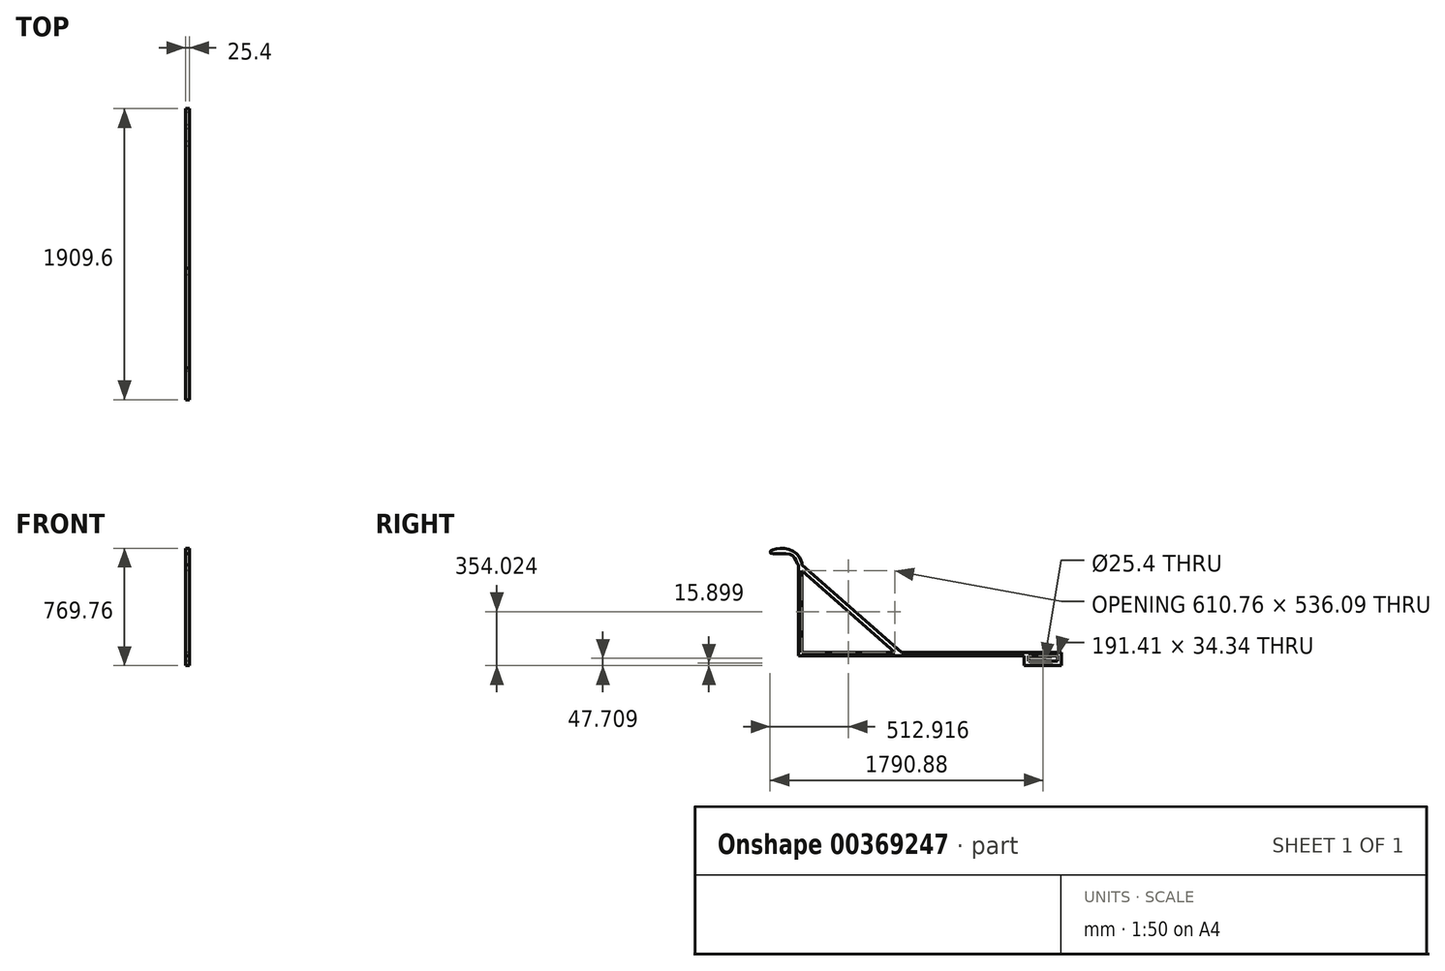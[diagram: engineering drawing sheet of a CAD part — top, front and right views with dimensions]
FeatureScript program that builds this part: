
annotation { "Feature Type Name" : "Feature", "Feature Type Description" : "" }
export const myFeature = defineFeature(function(context is Context, id is Id, definition is map)
    precondition{}
    {
        {
            var Q0;
            Q0=qCreatedBy(makeId("Right.planeOp"),FACE);
            var sketch = newSketch(context, id + "F0", { "sketchPlane" : qUnion([Q0])});
            skLineSegment(sketch, "E0.bottom", {"start": v(-864.8, -69.1) * mm, "end": v(613.39, -69.1) * mm});
            skLineSegment(sketch, "E0.top", {"start": v(-843.71, -48) * mm, "end": v(-232.95, -48) * mm});
            skLineSegment(sketch, "E0.left", {"start": v(-864.8, -69.1) * mm, "end": v(-864.8, -48) * mm});
            skLineSegment(sketch, "E0.right", {"start": v(858.35, -69.1) * mm, "end": v(858.35, -48) * mm});
            skLineSegment(sketch, "E1.left", {"start": v(-864.8, -48) * mm, "end": v(-864.8, 526.38) * mm});
            skLineSegment(sketch, "E1.right", {"start": v(-843.71, -48) * mm, "end": v(-843.71, 488.1) * mm});
            skLineSegment(sketch, "E2", {"start": v(-843.71, 526.38) * mm, "end": v(-189.33, -48) * mm});
            skLineSegment(sketch, "E3", {"start": v(-232.95, -48) * mm, "end": v(-843.71, 488.1) * mm});
            skLineSegment(sketch, "E4.trimOffspring", {"start": v(-189.33, -48) * mm, "end": v(858.35, -48) * mm});
            skLineSegment(sketch, "E5.top", {"start": v(858.35, -133.98) * mm, "end": v(835.33, -133.98) * mm});
            skLineSegment(sketch, "E5.left", {"start": v(858.35, -69.1) * mm, "end": v(858.35, -133.98) * mm});
            skLineSegment(sketch, "E5.right", {"start": v(835.33, -69.1) * mm, "end": v(835.33, -103.44) * mm});
            skLineSegment(sketch, "E6.bottom", {"start": v(835.33, -133.98) * mm, "end": v(643.92, -133.98) * mm});
            skLineSegment(sketch, "E6.top", {"start": v(835.33, -103.44) * mm, "end": v(643.92, -103.44) * mm});
            skLineSegment(sketch, "E7.bottom", {"start": v(643.92, -133.98) * mm, "end": v(613.39, -133.98) * mm});
            skLineSegment(sketch, "E7.left", {"start": v(643.92, -103.44) * mm, "end": v(643.92, -69.1) * mm});
            skLineSegment(sketch, "E7.right", {"start": v(613.39, -133.98) * mm, "end": v(613.39, -69.1) * mm});
            skLineSegment(sketch, "E8.trimOffspring", {"start": v(643.92, -69.1) * mm, "end": v(835.33, -69.1) * mm});
            skCircle(sketch, "E9", {"center": v(739.63, -118.08) * mm, "radius": 12.7 * mm});
            skPoint(sketch, "E9.centerSnap0", {"position": v(739.63, -133.98) * mm});
            skFitSpline(sketch, "E10", {"points": [v(-864.8, 526.38) * mm, v(-909.22, 591.88) * mm, v(-1046.38, 604.03) * mm, v(-1046.38, 619.66) * mm, v(-902.28, 617.92) * mm, v(-843.71, 526.38) * mm, v(-864.8, 526.38) * mm]});
            skSolve(sketch);
        }
        {
            var Q0;
            Q0 = qSketchRegion(id + "F0", true);
            extrude(context, id + "F1", {"entities" : qUnion([Q0]), "depth" : 25.4 * mm});
        }
    });
